# Revit family: Domotics-DomesticRanges-GEWISS-27COMBI22-IP66_ENCLOSURES_3OPERATORS_D22
name_source: partatom
category: Apparecchi elettrici
revit_build: Autodesk Revit 2016 (Build: 20161004_0715(x64)
units: mm (PartAtom-declared; Revit-internal decimal feet)

## family parameters
Condiviso = No
Host = Muro
Mantenere orientamento annotazione = No
Punto di calcolo locali = No
Quota connettore circolare = Usa diametro
Sempre verticale = Sì
Taglio con vuoti quando caricato = No
Tipo di parte = Normale

## types (1)
- Domotics-DomesticRanges-GEWISS-27COMBI22-IP66_ENCLOSURES_3OPERATORS_D22
    Altezza = 171 mm  [stored 0.561024 ft]
    Catalogue = DOMOTICS
    Catalogue Range = 27COMBI
    Colour = Grey RAL 7035
    Descrizione = ENCLOSURE 3G START-STOP-IND.BUTTON
    EAN code = 8011564055599
    Electrocod = 0212
    Glow Wire Test = 650°C
    IDF = 04ee00b3-4694-4f23-b7aa-444eda168778
    IDT = eb43bfa2-97ff-42a8-b7a2-23da41b5a658
    IP degree = IP66
    Immagine tipo = GW27204.jpg
    Installation temperature = -25 +60 °C
    Insulation class = II
    Larghezza = 82 mm  [stored 0.269029 ft]
    Lid screws = Stainless steel
    Modello = GW27204
    No. gangs = 3
    Operators Ã˜ 22 = Start, stop, indicator
    Outer dim. LxHxD (mm) = 66x171x65
    Produttore = GEWISS S.p.A.
    Profondità = 65 mm
    Pulsante_1 = Pulsante marcia -verde
    Pulsante_2 = Pulsante arresto - rosso
    Pulsante_3 = Pulsante segnalazione - grigio
    SEO = Enclosure
    Standard = EN 60947-1 - EN 60947-5-1
    Standard; = EN 60947-1 - EN 60947-5-1
    Technical sheet = https://www.gewiss.com
    Thermo-pressure with ball = 70
    Torque screws tightening = 0,8NM
    Type of knockout holes = Removable with tool
    URL = https://www.gewiss.com
    Version file RFA = 18.0

note: source unit labels omitted for Thermo-pressure with ball — the stored unit's dimension contradicts the parameter name (converter mislabeling)

note: [stored X ft] marks values corroborated as IEEE doubles in the binary element streams (Revit-internal decimal feet)
